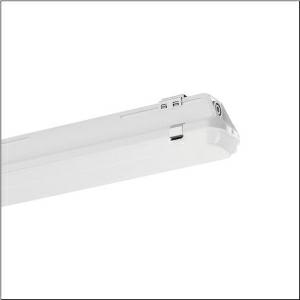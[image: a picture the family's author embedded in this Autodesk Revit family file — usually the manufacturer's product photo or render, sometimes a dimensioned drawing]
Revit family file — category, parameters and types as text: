
# Revit family: monsun_r__21_51fb12mp480b_d2d7
name_source: partatom
category: Lighting Fixtures
units: mm (PartAtom-declared; Revit-internal decimal feet)

## family parameters
Cut with Voids When Loaded = No
Host = Face
Light Source = No
Part Type = Normal
Room Calculation Point = No
Round Connector Dimension = Use Diameter
Shared = No

## types (1)
- --- (1 x LED, 8100 lm, 53.6 W, 4000K)
    Apparent Load = 54 VA
    CIE Flux Codes = 65 88 97 97 100
    Color Rendering = 80
    Color Temperature = 4000K
    Default Elevation = 1800 mm
    Description = Monsun® 21, damp-proof luminaire, chain hanger, primary light control with lens, primary optical cover: enclosure, of PMMA, light emission: direct distribution, primary light characteristic: symmetric, installation type: suspended mounting, surface-mounted, horizontal mounting, vertical mounting, LED, rated luminous flux: 8.100lm, luminous efficacy: 151lm/W, light colour: 840, colour temperature: 4000K, control gear: ECG, with terminal, 3-pole, max. 2.5mm², mains connection: 220..240V, AC, 50/60Hz, rated input power: 54W, housing, of glass-fibre reinforced polyester, uncoated, bright grey, length: 1.590mm, width: 90mm, height: 88mm, clip for enclosure, of stainless steel (V2A), ceiling mounting element, of stainless steel (V2A), chain hanger, of stainless steel (V2A), protection rating (complete): IP66, insulation class (complete): insulation class I (protective earthing), certification: CE, ENEC, VDE, UKCA, protection symbol: D, impact resistance: IK04, permissible operating ambient temperature: -25..+35°C, standard: EN 50419, EN 60598-2-1, corresponds to IFS (International Featured Standards) requirements for safety and quality in the food industry, for indoor or canopied outdoor use, no direct snow, no direct sun, no direct rain, packaging unit: 1 piece
    Height = 89 mm
    Lamp = 1 x LED
    Lamp Light Flux = 8100 lm
    Lamp Power = 53.6 W
    Lamp count = 1
    Length = 1590 mm
    Luminous efficacy = 151 lm/W
    Manufacturer = Siteco
    ModVariant = No
    Model = 51FB12MP480B
    Mounting Place = Ceiling
    Mounting Type = Pendant
    Number of Poles = 1
    OnlyDefault = Yes
    Power Factor = 1
    Product Name = Monsun® 21
    Product group = damp-proof luminaire | ceiling pendant
    ProductGroupID = 908
    Protection Class = Protection class I
    Protection Degree = IP 66
    RLX_Detail_Level = 1
    RlxData = <blob elided: 89333 chars, md5=8eb9fa10>
    Socket = socket
    Standby Power = 0 W
    System Light Flux = 8100 lm
    System Power = 54 W
    Type Comments = factory setting: luminous flux: 100 % | (A | C | E) | 121 mA
    Type Image = l_1006717.jpg
    URL = http://relux.com
    VarID = @adj_056867
    Voltage = 0 V
    Weight = 0.00 kg
    Width = 90 mm

## geometry (parser evidence)
native form markers: Blend x4, Sweep x9
no freeform markers — native parametric forms only
